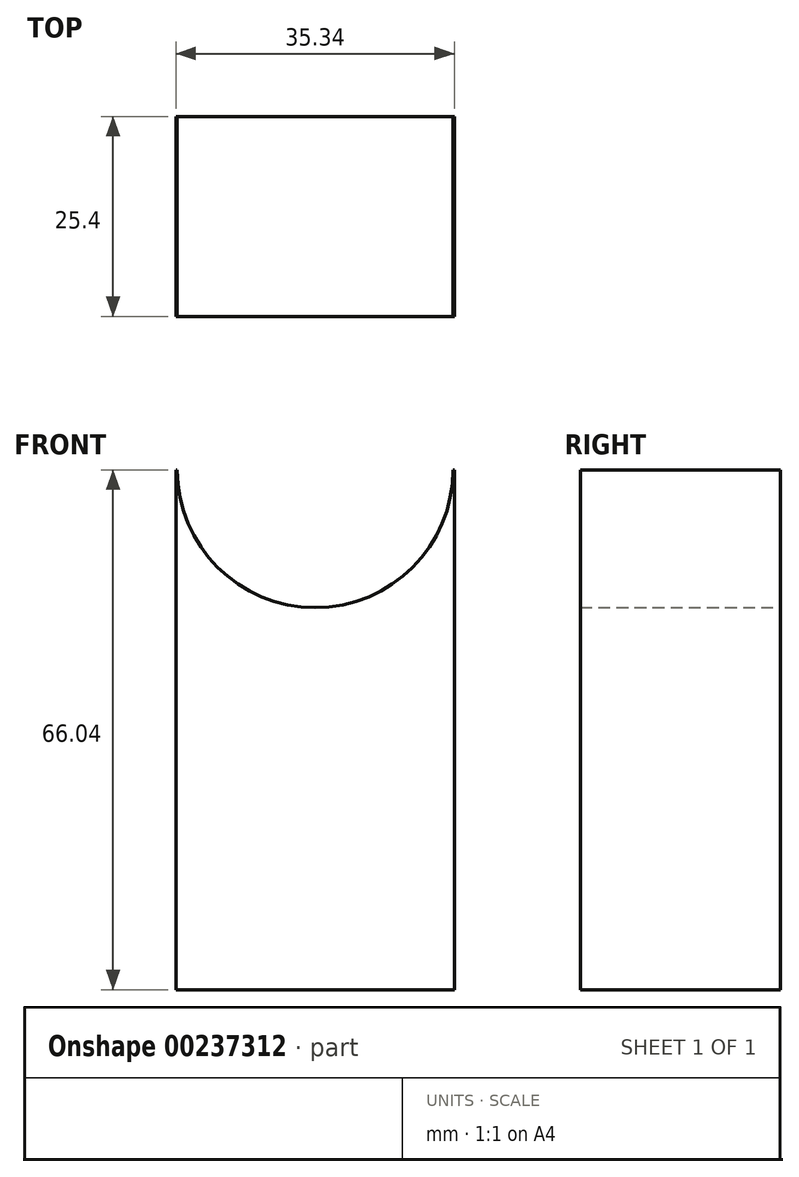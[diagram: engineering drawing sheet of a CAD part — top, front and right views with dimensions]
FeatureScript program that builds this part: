
annotation { "Feature Type Name" : "Feature", "Feature Type Description" : "" }
export const myFeature = defineFeature(function(context is Context, id is Id, definition is map)
    precondition{}
    {
        {
            var Q0;
            Q0=qCreatedBy(makeId("Front.planeOp"),FACE);
            var sketch = newSketch(context, id + "F0", { "sketchPlane" : qUnion([Q0])});
            skLineSegment(sketch, "E0.bottom", {"start": v(-17.67, 33.02) * mm, "end": v(17.67, 33.02) * mm});
            skLineSegment(sketch, "E0.top", {"start": v(-17.67, -33.02) * mm, "end": v(17.67, -33.02) * mm});
            skLineSegment(sketch, "E0.left", {"start": v(-17.67, 33.02) * mm, "end": v(-17.67, -33.02) * mm});
            skLineSegment(sketch, "E0.right", {"start": v(17.67, 33.02) * mm, "end": v(17.67, -33.02) * mm});
            skPoint(sketch, "E0.middle", {"position": v(0, 0) * mm});
            skCircle(sketch, "E1", {"center": v(0, 33.02) * mm, "radius": 17.51 * mm});
            skCircle(sketch, "E2", {"center": v(0, 33.02) * mm, "radius": 8.15 * mm});
            skSolve(sketch);
        }
        {
            var Q0;
            {var subQ0=sQuery(id+"F0.wireOp",EDGE,"E1");var subQ1=sQuery(id+"F0.wireOp",EDGE,"E0.bottom");var subQ2=makeQuery(id+"F0.imprint","INTERSECT",VERTEX,{"disambiguationData":[OD(0.0)],"derivedFrom":[subQ1,subQ0]});Q0=makeQuery(id+"F0.imprint","IMPRINT",FACE,{"disambiguationData":[TD([[makeQuery(id+"F0.imprint","IMPRINT",EDGE,{"disambiguationData":[TD([[subQ2,-1.0]])],"derivedFrom":subQ1}),-1.0]])]});}
            var Q1;
            {var subQ0=sQuery(id+"F0.wireOp",EDGE,"E1");var subQ1=sQuery(id+"F0.wireOp",EDGE,"E0.bottom");var subQ2=makeQuery(id+"F0.imprint","INTERSECT",VERTEX,{"disambiguationData":[OD(0.0)],"derivedFrom":[subQ1,subQ0]});Q1=makeQuery(id+"F0.imprint","IMPRINT",FACE,{"disambiguationData":[TD([[makeQuery(id+"F0.imprint","IMPRINT",EDGE,{"disambiguationData":[TD([[subQ2,-1.0]])],"derivedFrom":subQ1}),1.0]])]});}
            var Q2;
            Q2=makeQuery(id+"F0.imprint","IMPRINT",FACE,{"disambiguationData":[TD([[makeQuery(id+"F0.imprint","IMPRINT",EDGE,{"derivedFrom":sQuery(id+"F0.wireOp",EDGE,"E0.top")}),1.0]])]});
            extrude(context, id + "F1", {"entities" : qUnion([Q0, Q1, Q2]), "depth" : 25.4 * mm});
        }
    });
